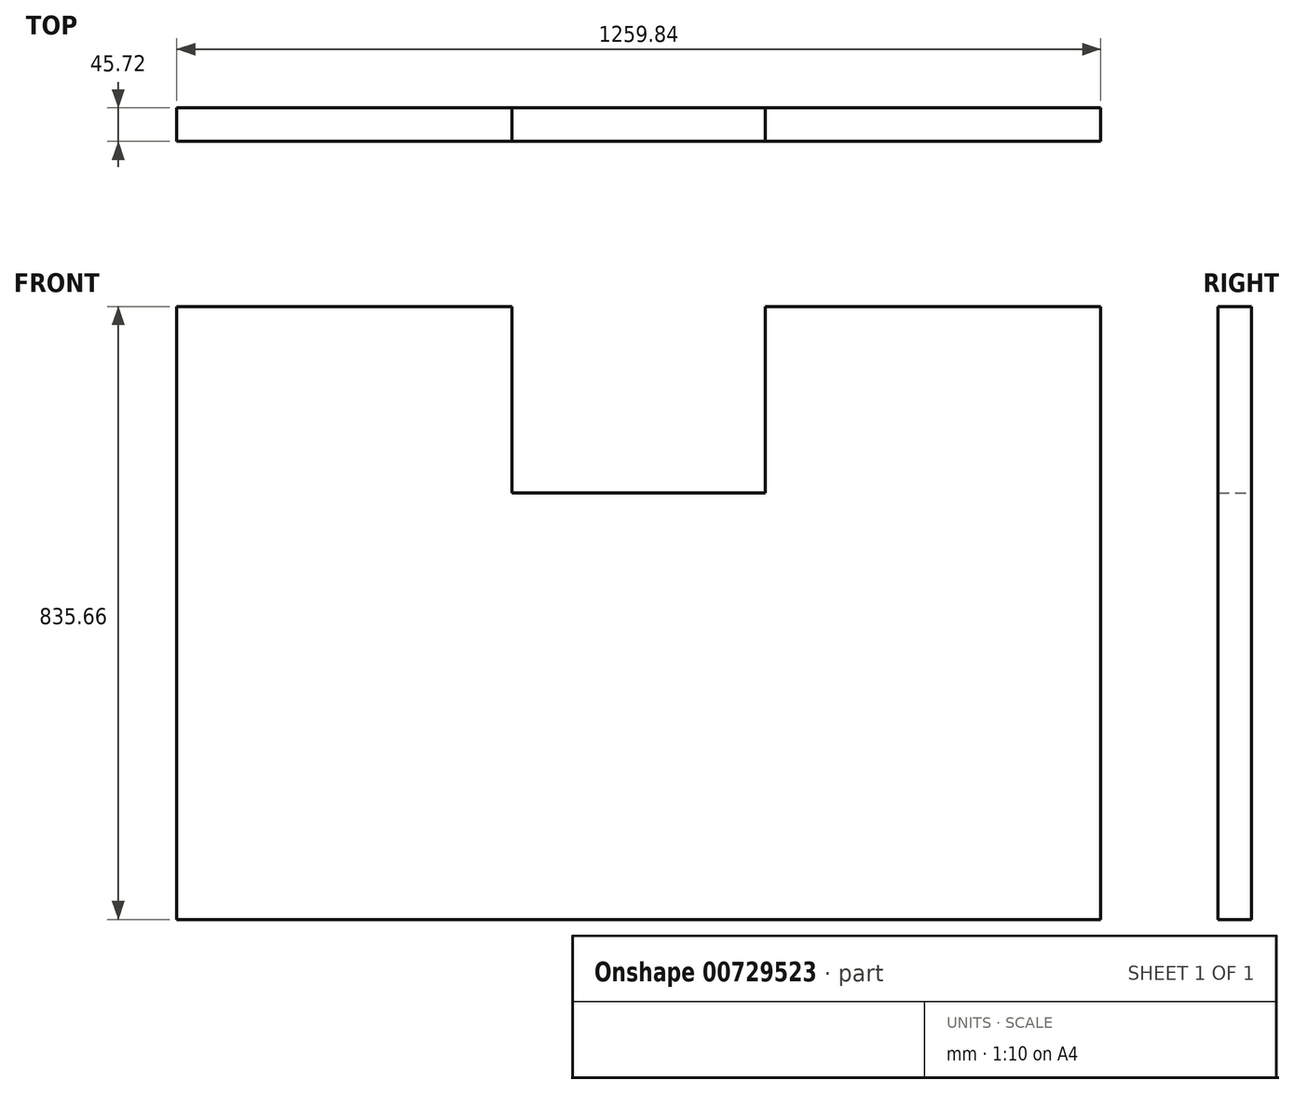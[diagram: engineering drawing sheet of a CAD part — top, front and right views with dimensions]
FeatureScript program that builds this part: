
annotation { "Feature Type Name" : "Feature", "Feature Type Description" : "" }
export const myFeature = defineFeature(function(context is Context, id is Id, definition is map)
    precondition{}
    {
        {
            var Q0;
            Q0=qCreatedBy(makeId("Front.planeOp"),FACE);
            var sketch = newSketch(context, id + "F0", { "sketchPlane" : qUnion([Q0])});
            skLineSegment(sketch, "E0", {"start": v(0, 0) * mm, "end": v(0, 835.66) * mm});
            skLineSegment(sketch, "E1", {"start": v(457.2, 835.66) * mm, "end": v(0, 835.66) * mm});
            skLineSegment(sketch, "E2", {"start": v(457.2, 835.66) * mm, "end": v(457.2, 581.66) * mm});
            skLineSegment(sketch, "E3", {"start": v(457.2, 581.66) * mm, "end": v(802.64, 581.66) * mm});
            skLineSegment(sketch, "E4", {"start": v(802.64, 581.66) * mm, "end": v(802.64, 835.66) * mm});
            skLineSegment(sketch, "E5", {"start": v(802.64, 835.66) * mm, "end": v(1259.84, 835.66) * mm});
            skLineSegment(sketch, "E6", {"start": v(1259.84, 835.66) * mm, "end": v(1259.84, 0) * mm});
            skLineSegment(sketch, "E7", {"start": v(1259.84, 0) * mm, "end": v(0, 0) * mm});
            skSolve(sketch);
        }
        {
            var Q0;
            Q0 = qSketchRegion(id + "F0", true);
            extrude(context, id + "F1", {"entities" : qUnion([Q0]), "depth" : 45.72 * mm, "offsetDistance" : 25.4 * mm});
        }
    });
